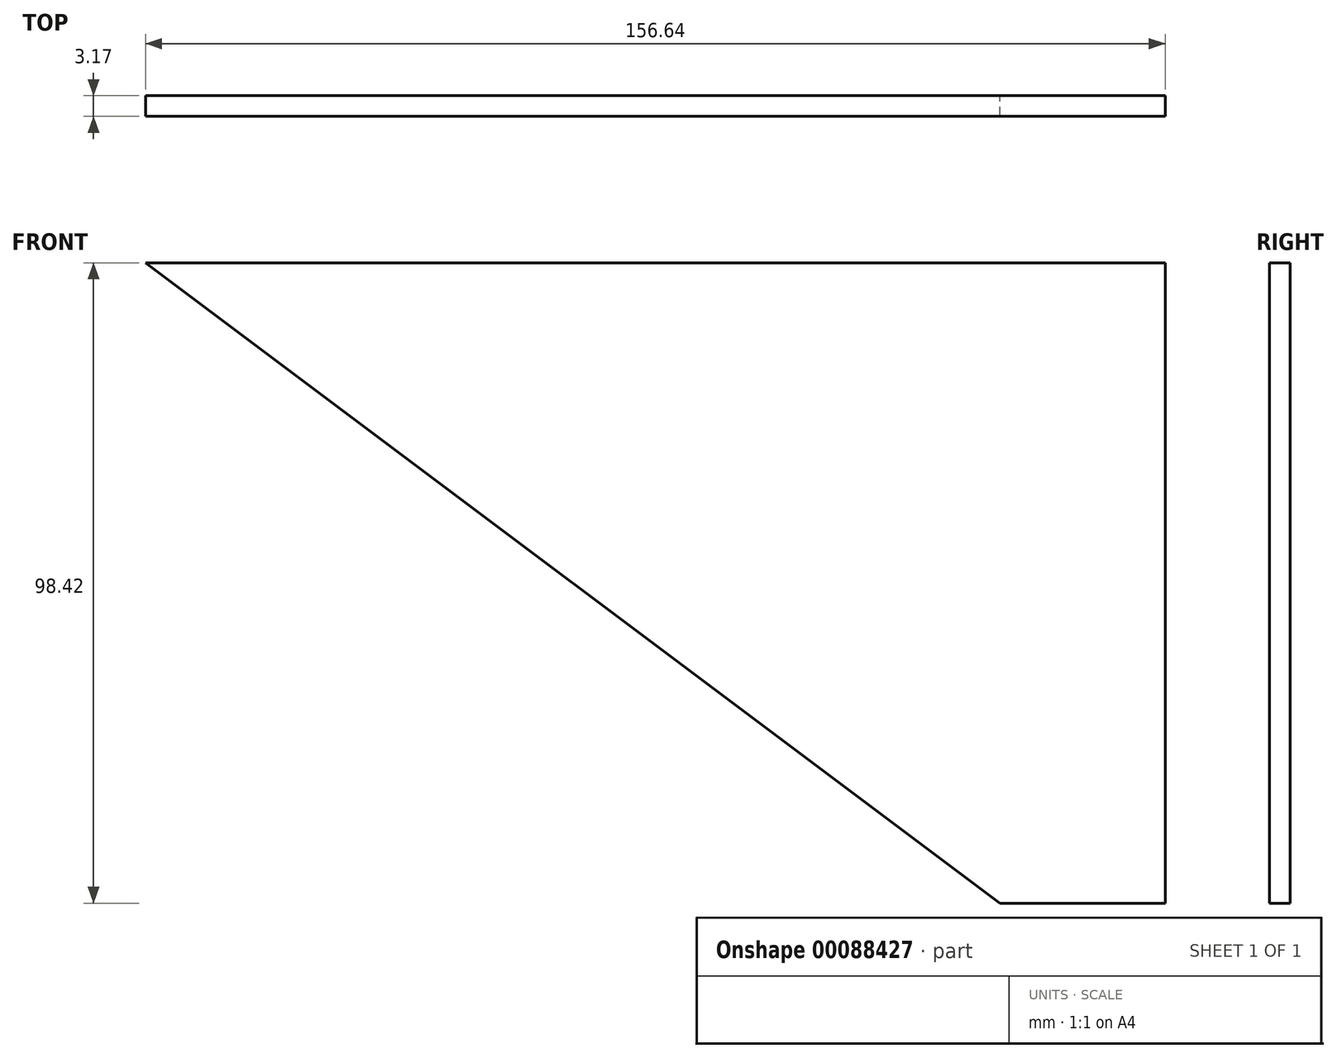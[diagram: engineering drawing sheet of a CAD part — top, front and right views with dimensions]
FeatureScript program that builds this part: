
annotation { "Feature Type Name" : "Feature", "Feature Type Description" : "" }
export const myFeature = defineFeature(function(context is Context, id is Id, definition is map)
    precondition{}
    {
        {
            var Q0;
            Q0=qCreatedBy(makeId("Front.planeOp"),FACE);
            var sketch = newSketch(context, id + "F0", { "sketchPlane" : qUnion([Q0])});
            skLineSegment(sketch, "E0", {"start": v(0, 0) * mm, "end": v(156.64, 0) * mm});
            skLineSegment(sketch, "E1", {"start": v(156.64, 0) * mm, "end": v(156.64, -98.43) * mm});
            skLineSegment(sketch, "E2", {"start": v(156.64, -98.43) * mm, "end": v(131.24, -98.43) * mm});
            skLineSegment(sketch, "E3", {"start": v(131.24, -98.43) * mm, "end": v(0, 0) * mm});
            skSolve(sketch);
        }
        {
            var Q0;
            Q0=makeQuery(id+"F0.imprint","IMPRINT",FACE,{"disambiguationData":[TD([[makeQuery(id+"F0.imprint","IMPRINT",EDGE,{"derivedFrom":sQuery(id+"F0.wireOp",EDGE,"E0")}),-1.0]])]});
            extrude(context, id + "F1", {"entities" : qUnion([Q0]), "depth" : 3.17 * mm});
        }
    });
